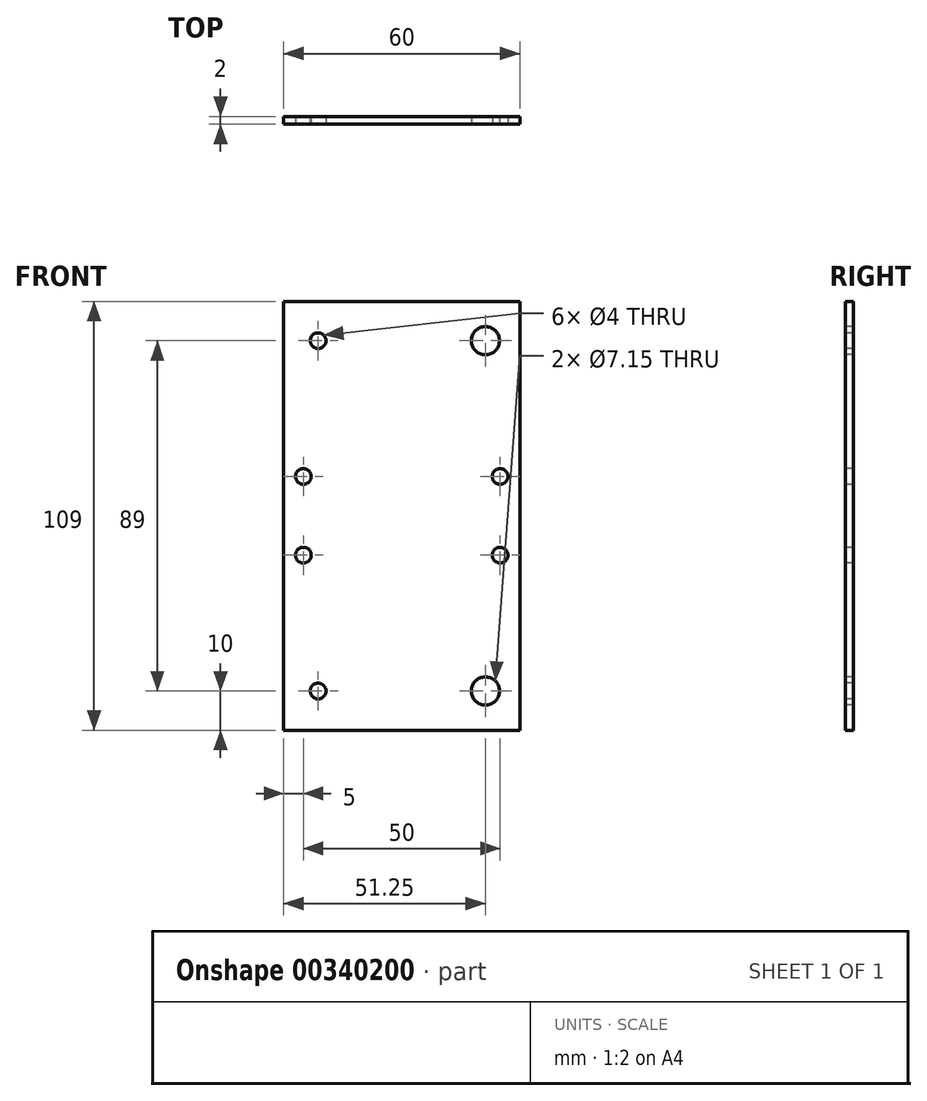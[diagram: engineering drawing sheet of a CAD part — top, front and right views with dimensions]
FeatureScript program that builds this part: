
annotation { "Feature Type Name" : "Feature", "Feature Type Description" : "" }
export const myFeature = defineFeature(function(context is Context, id is Id, definition is map)
    precondition{}
    {
        {
            var Q0;
            Q0=qCreatedBy(makeId("Front.planeOp"),FACE);
            var sketch = newSketch(context, id + "F0", { "sketchPlane" : qUnion([Q0])});
            skLineSegment(sketch, "E0.bottom", {"start": v(30, 54.5) * mm, "end": v(-30, 54.5) * mm});
            skLineSegment(sketch, "E0.top", {"start": v(30, -54.5) * mm, "end": v(-30, -54.5) * mm});
            skLineSegment(sketch, "E0.left", {"start": v(30, 54.5) * mm, "end": v(30, -54.5) * mm});
            skLineSegment(sketch, "E0.right", {"start": v(-30, 54.5) * mm, "end": v(-30, -54.5) * mm});
            skPoint(sketch, "E0.middle", {"position": v(0, 0) * mm});
            skSolve(sketch);
        }
        {
            var Q0;
            Q0=qSketchRegion(id+"F0",true);
            extrude(context, id + "F1", {"entities" : qUnion([Q0]), "depth" : 2 * mm});
        }
        {
            var Q0;
            Q0=makeQuery(id+"F1.opExtrude","CAP_FACE",FACE,{"disambiguationData":[OSD([sQuery(id+"F0.wireOp",EDGE,"E0.bottom"),sQuery(id+"F0.wireOp",EDGE,"E0.top"),sQuery(id+"F0.wireOp",EDGE,"E0.left"),sQuery(id+"F0.wireOp",EDGE,"E0.right")])],"isStart":false});
            var sketch = newSketch(context, id + "F2", { "sketchPlane" : qUnion([Q0])});
            skLineSegment(sketch, "E1.bottom", {"start": v(21.25, 44.5) * mm, "end": v(-21.25, 44.5) * mm, "construction": true});
            skLineSegment(sketch, "E1.top", {"start": v(21.25, -44.5) * mm, "end": v(-21.25, -44.5) * mm, "construction": true});
            skLineSegment(sketch, "E1.left", {"start": v(21.25, 44.5) * mm, "end": v(21.25, -44.5) * mm, "construction": true});
            skLineSegment(sketch, "E1.right", {"start": v(-21.25, 44.5) * mm, "end": v(-21.25, -44.5) * mm, "construction": true});
            skPoint(sketch, "E1.middle", {"position": v(0, 0) * mm});
            skCircle(sketch, "E2", {"center": v(-21.25, 44.5) * mm, "radius": 2 * mm});
            skCircle(sketch, "E3", {"center": v(-21.25, -44.5) * mm, "radius": 2 * mm});
            skCircle(sketch, "E4", {"center": v(21.25, 44.5) * mm, "radius": 3.58 * mm});
            skCircle(sketch, "E5", {"center": v(21.25, -44.5) * mm, "radius": 3.58 * mm});
            skSolve(sketch);
        }
        {
            var Q0;
            Q0=qSketchRegion(id+"F2",true);
            extrude(context, id + "F3", {"entities" : qUnion([Q0]), "operationType" : NewBodyOperationType.REMOVE, "endBound" : BoundingType.UP_TO_NEXT, "oppositeDirection" : true, "depth" : 25 * mm});
        }
        {
            var Q0;
            Q0=makeQuery(id+"F1.opExtrude","CAP_FACE",FACE,{"disambiguationData":[OSD([sQuery(id+"F0.wireOp",EDGE,"E0.bottom"),sQuery(id+"F0.wireOp",EDGE,"E0.top"),sQuery(id+"F0.wireOp",EDGE,"E0.left"),sQuery(id+"F0.wireOp",EDGE,"E0.right")])],"isStart":false});
            var sketch = newSketch(context, id + "F4", { "sketchPlane" : qUnion([Q0])});
            skLineSegment(sketch, "E6.bottom", {"start": v(25, -10) * mm, "end": v(-25, -10) * mm, "construction": true});
            skLineSegment(sketch, "E6.top", {"start": v(25, 10) * mm, "end": v(-25, 10) * mm, "construction": true});
            skLineSegment(sketch, "E6.left", {"start": v(25, -10) * mm, "end": v(25, 10) * mm, "construction": true});
            skLineSegment(sketch, "E6.right", {"start": v(-25, -10) * mm, "end": v(-25, 10) * mm, "construction": true});
            skPoint(sketch, "E6.middle", {"position": v(0, 0) * mm});
            skCircle(sketch, "E7", {"center": v(-25, 10) * mm, "radius": 2 * mm});
            skCircle(sketch, "E8", {"center": v(25, 10) * mm, "radius": 2 * mm});
            skCircle(sketch, "E9", {"center": v(-25, -10) * mm, "radius": 2 * mm});
            skCircle(sketch, "E10", {"center": v(25, -10) * mm, "radius": 2 * mm});
            skSolve(sketch);
        }
        {
            var Q0;
            Q0=qSketchRegion(id+"F4",true);
            extrude(context, id + "F5", {"entities" : qUnion([Q0]), "operationType" : NewBodyOperationType.REMOVE, "endBound" : BoundingType.UP_TO_NEXT, "oppositeDirection" : true, "depth" : 25 * mm});
        }
    });
